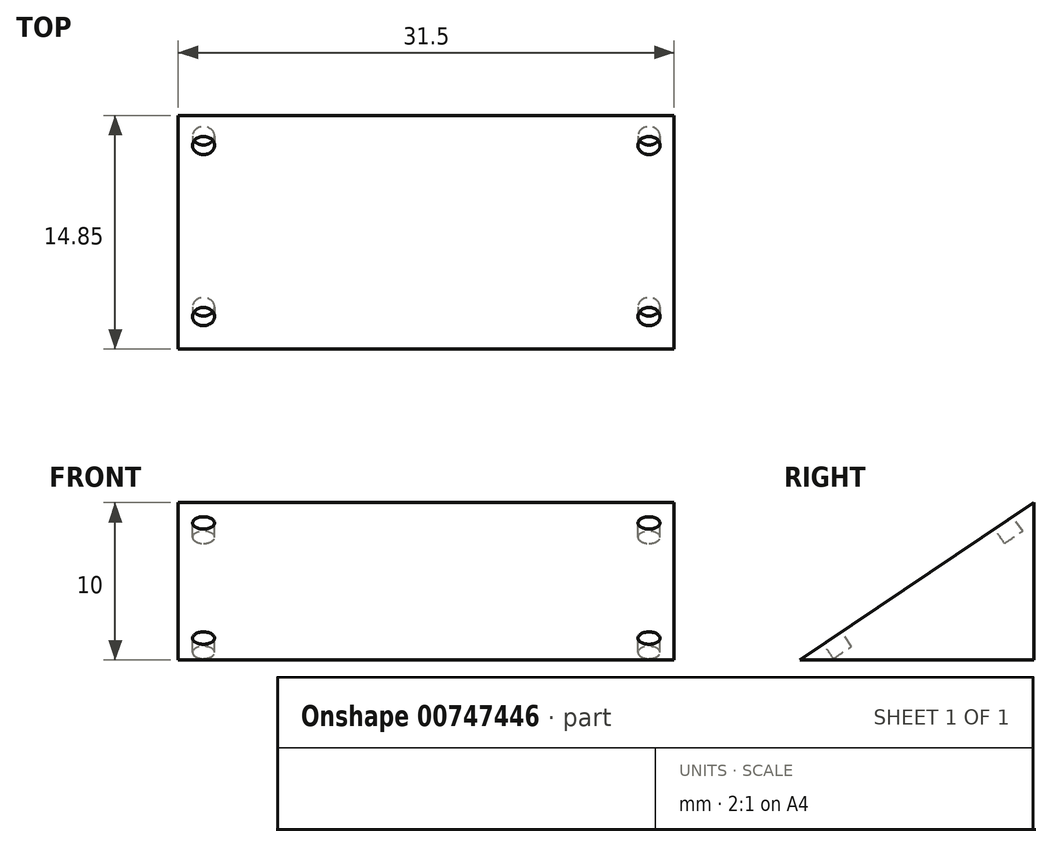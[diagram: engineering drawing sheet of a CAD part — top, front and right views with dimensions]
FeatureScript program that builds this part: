
annotation { "Feature Type Name" : "Feature", "Feature Type Description" : "" }
export const myFeature = defineFeature(function(context is Context, id is Id, definition is map)
    precondition{}
    {
        {
            var Q0;
            Q0=qCreatedBy(makeId("Right.planeOp"),FACE);
            var sketch = newSketch(context, id + "F0", { "sketchPlane" : qUnion([Q0])});
            skLineSegment(sketch, "E0", {"start": v(14.85, 10) * mm, "end": v(0, 0) * mm});
            skLineSegment(sketch, "E1", {"start": v(14.85, 10) * mm, "end": v(14.85, 0) * mm});
            skLineSegment(sketch, "E2", {"start": v(14.85, 0) * mm, "end": v(0, 0) * mm});
            skSolve(sketch);
        }
        {
            var Q0;
            Q0=makeQuery(id+"F0.imprint","IMPRINT",FACE,{"disambiguationData":[TD([[makeQuery(id+"F0.imprint","IMPRINT",EDGE,{"derivedFrom":sQuery(id+"F0.wireOp",EDGE,"E0")}),1.0]])]});
            extrude(context, id + "F1", {"entities" : qUnion([Q0]), "depth" : 31.5 * mm, "offsetDistance" : 25 * mm});
        }
        {
            var Q0;
            Q0=makeQuery(id+"F1.opExtrude","SWEPT_FACE",FACE,{"disambiguationData":[OSD([sQuery(id+"F0.wireOp",EDGE,"E0")])]});
            var sketch = newSketch(context, id + "F2", { "sketchPlane" : qUnion([Q0])});
            skCircle(sketch, "E3", {"center": v(1.6, 15.6) * mm, "radius": 0.7 * mm});
            skCircle(sketch, "E4", {"center": v(29.9, 15.6) * mm, "radius": 0.7 * mm});
            skCircle(sketch, "E5", {"center": v(29.9, 2.5) * mm, "radius": 0.7 * mm});
            skCircle(sketch, "E6", {"center": v(1.6, 2.5) * mm, "radius": 0.7 * mm});
            skSolve(sketch);
        }
        {
            var Q0;
            Q0=makeQuery(id+"F2.imprint","IMPRINT",FACE,{"disambiguationData":[TD([[makeQuery(id+"F2.imprint","IMPRINT",EDGE,{"derivedFrom":sQuery(id+"F2.wireOp",EDGE,"E3")}),1.0]])]});
            var Q1;
            Q1=makeQuery(id+"F2.imprint","IMPRINT",FACE,{"disambiguationData":[TD([[makeQuery(id+"F2.imprint","IMPRINT",EDGE,{"derivedFrom":sQuery(id+"F2.wireOp",EDGE,"E4")}),1.0]])]});
            var Q2;
            Q2=makeQuery(id+"F2.imprint","IMPRINT",FACE,{"disambiguationData":[TD([[makeQuery(id+"F2.imprint","IMPRINT",EDGE,{"derivedFrom":sQuery(id+"F2.wireOp",EDGE,"E5")}),1.0]])]});
            var Q3;
            Q3=makeQuery(id+"F2.imprint","IMPRINT",FACE,{"disambiguationData":[TD([[makeQuery(id+"F2.imprint","IMPRINT",EDGE,{"derivedFrom":sQuery(id+"F2.wireOp",EDGE,"E6")}),1.0]])]});
            var Q4;
            Q4=sQuery(id+"F2.wireOp",EDGE,"E3");
            var Q5;
            Q5=sQuery(id+"F2.wireOp",EDGE,"E4");
            var Q6;
            Q6=sQuery(id+"F2.wireOp",EDGE,"E5");
            var Q7;
            Q7=sQuery(id+"F2.wireOp",EDGE,"E6");
            extrude(context, id + "F3", {"entities" : qUnion([Q0, Q1, Q2, Q3]), "operationType" : NewBodyOperationType.REMOVE, "surfaceEntities" : qUnion([Q4, Q5, Q6, Q7]), "oppositeDirection" : true, "depth" : 1.1 * mm, "offsetDistance" : 25 * mm});
        }
    });
